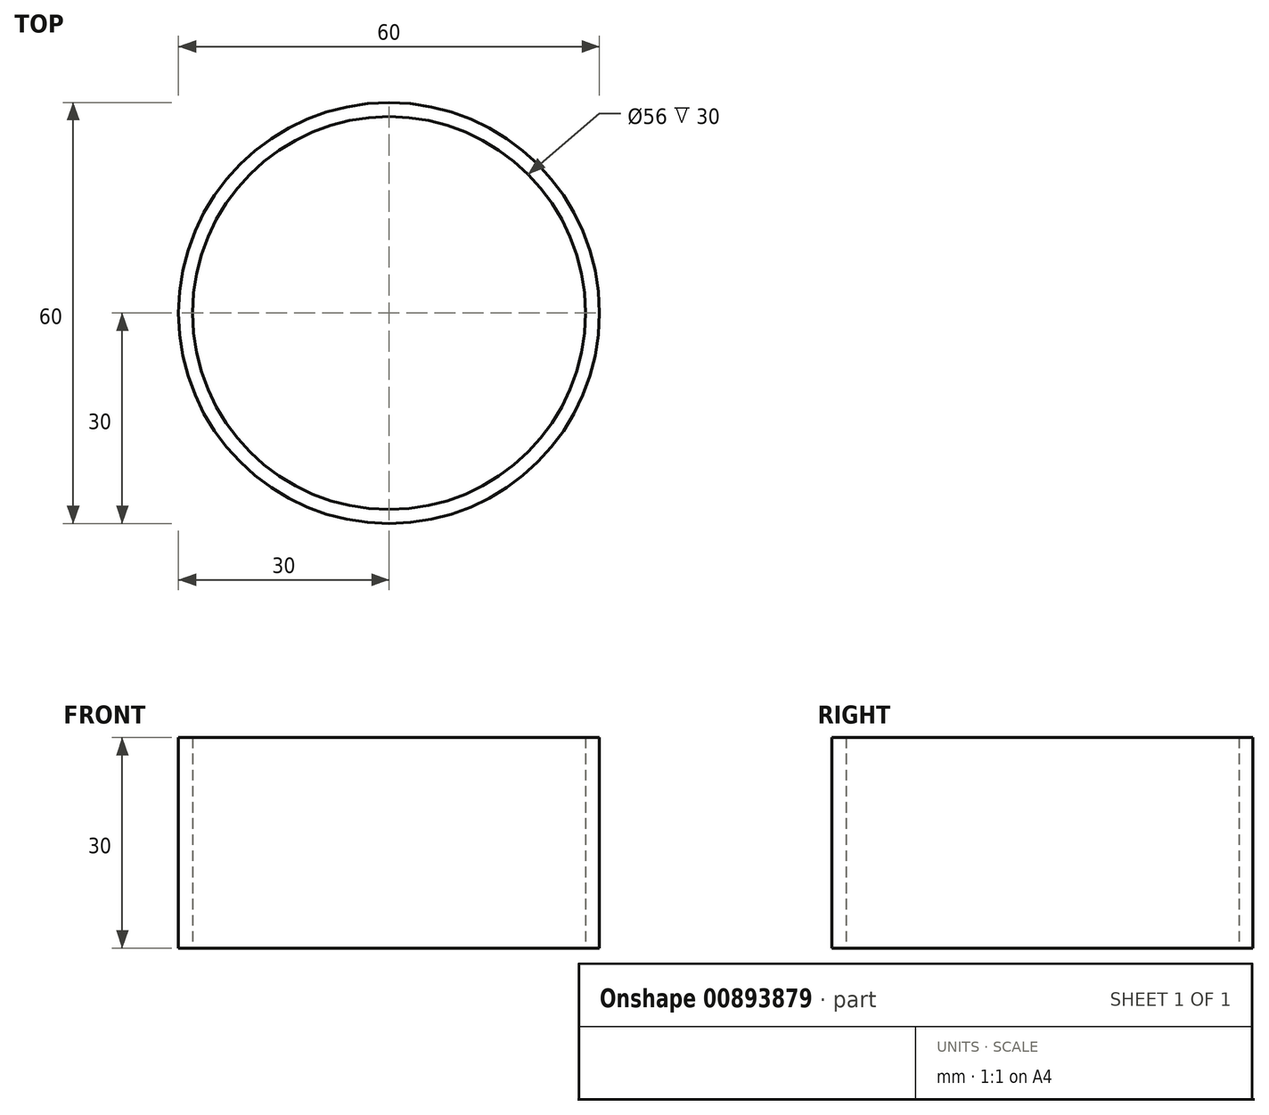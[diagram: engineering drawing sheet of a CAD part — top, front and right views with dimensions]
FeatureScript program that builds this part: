
annotation { "Feature Type Name" : "Feature", "Feature Type Description" : "" }
export const myFeature = defineFeature(function(context is Context, id is Id, definition is map)
    precondition{}
    {
        {
            var Q0;
            Q0=qCreatedBy(makeId("Top.planeOp"),FACE);
            var sketch = newSketch(context, id + "F0", { "sketchPlane" : qUnion([Q0])});
            skCircle(sketch, "E0", {"center": v(0, 0) * mm, "radius": 30 * mm});
            skCircle(sketch, "E1", {"center": v(0, 0) * mm, "radius": 28 * mm});
            skSolve(sketch);
        }
        {
            var Q0;
            Q0=makeQuery(id+"F0.imprint","IMPRINT",FACE,{"disambiguationData":[TD([[makeQuery(id+"F0.imprint","IMPRINT",EDGE,{"derivedFrom":sQuery(id+"F0.wireOp",EDGE,"E0")}),1.0]])]});
            extrude(context, id + "F1", {"entities" : qUnion([Q0]), "depth" : 30 * mm, "offsetDistance" : 25 * mm});
        }
    });
